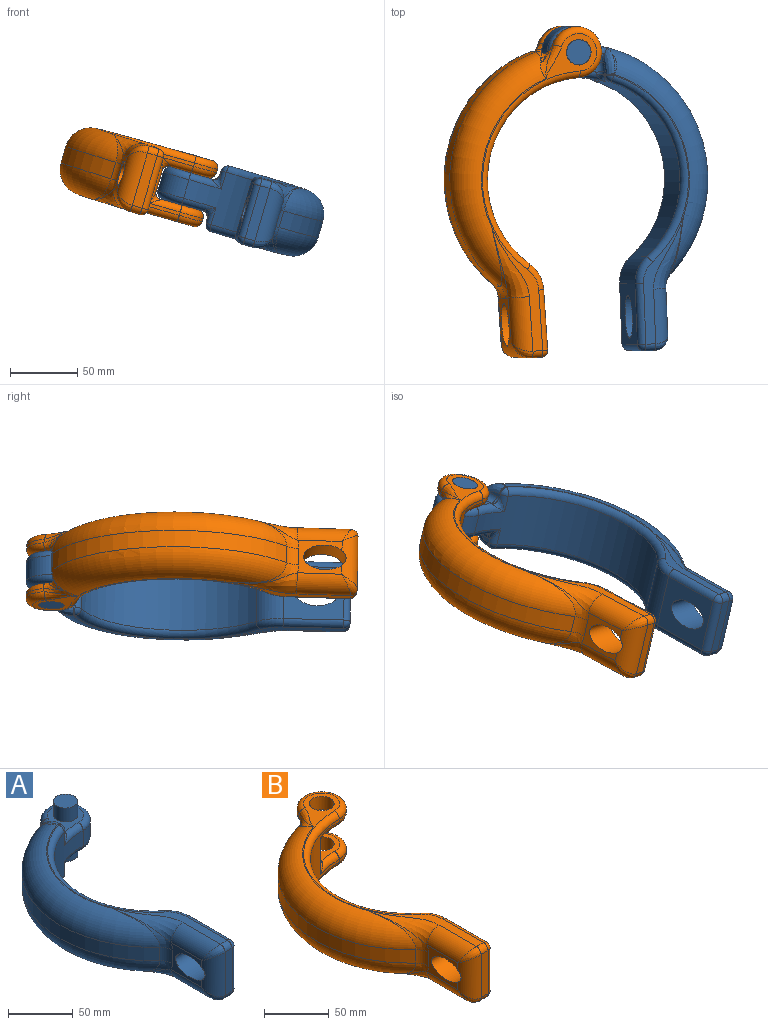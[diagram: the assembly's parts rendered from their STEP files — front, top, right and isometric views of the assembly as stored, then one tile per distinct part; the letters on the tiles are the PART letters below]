
ASSEMBLY  parts=2 mates=1
PART A: 72 faces, bbox 130.1x245.4x76.2 mm
  f0: bspline ~8.17x6.54mm, area 11.9mm2, adj f5,f15,f17,f42
  f1: bspline ~24.13x21.85mm, area 0mm2, adj f16,f52
  f2: plane 202.03x55.42mm, normal (0,0,1), area 673.6mm2, adj f8,f16,f21,f23,f26,f33,f35,f50
  f3: plane 202.03x55.42mm, normal (0,0,-1), area 673.6mm2, adj f9,f15,f18,f20,f28,f30,f37,f57
  f4: cylinder r=76.2mm len=135.68mm, axis (0,0,-1), area 6970.8mm2, adj f5,f8,f9,f36,f44,f47,f48,f53
  f5: cylinder r=19.05mm len=38.1mm, axis (0,0,-1), area 1159.1mm2, adj f0,f4,f7,f17,f43,f46
  f6: bspline ~24.13x21.85mm, area 0mm2, adj f15,f54
  f7: bspline ~8.17x6.54mm, area 10.7mm2, adj f5,f16,f17,f45
  f8: torus R=81.28mm, axis (0,0,1), area 1328mm2, adj f2,f4,f35,f49
  f9: torus R=81.28mm, axis (0,0,1), area 1328mm2, adj f3,f4,f37,f55
  f10: plane 45.1x40.64mm, normal (1,0,0), area 1347.7mm2, adj f14,f26,f27,f28,f36
  f11: cylinder r=101.12mm len=173.13mm, axis (0,0,-1), area 2773.9mm2, adj f15,f16,f17,f24
  f12: plane 33.12x25.41mm, normal (-1,0,0), area 362.8mm2, adj f14,f18,f19,f21,f22,f24,f25
  f13: plane 40.64x7.62mm, normal (0,-1,0), area 309.7mm2, adj f19,f27,f30,f33
  f14: extruded ~31.75x25.4mm, area 2069.9mm2, adj f10,f12,f19
  f15: torus R=82.07mm, axis (0,0,1), area 5601.8mm2, adj f0,f3,f6,f11,f22,f42,f54,f56
  f16: torus R=82.07mm, axis (0,0,1), area 5601.6mm2, adj f1,f2,f7,f11,f25,f45,f51,f52
  f17: cylinder r=12.7mm len=12.7mm, axis (0,0,1), area 133.5mm2, adj f0,f5,f7,f11
  f18: cylinder r=12.7mm len=40.73mm, axis (0,-1,0), area 736.6mm2, adj f3,f12,f20,f29
  f19: cylinder r=12.7mm len=40.64mm, axis (0,0,-1), area 640mm2, adj f12,f13,f14,f29,f32
  f20: bspline ~56.17x25.4mm, area 0mm2, adj f3,f18,f22
  f21: cylinder r=12.7mm len=40.73mm, axis (0,1,0), area 736.6mm2, adj f2,f12,f23,f32
  f22: bspline ~56.94x34.14mm, area 144.1mm2, adj f12,f15,f20,f24
  f23: bspline ~56.17x25.4mm, area 342.2mm2, adj f2,f21,f25
  f24: cylinder r=12.7mm len=12.7mm, axis (0,0,-1), area 135mm2, adj f11,f12,f22,f25
  f25: bspline ~56.94x34.14mm, area 144.1mm2, adj f12,f16,f23,f24
  f26: cylinder r=5.08mm len=45.1mm, axis (0,-1,0), area 359.9mm2, adj f2,f10,f34,f35
  f27: cylinder r=5.08mm len=40.64mm, axis (0,0,-1), area 324.3mm2, adj f10,f13,f31,f34
  f28: cylinder r=5.08mm len=45.1mm, axis (0,1,0), area 359.9mm2, adj f3,f10,f31,f37
  f29: bspline ~13.28x12.7mm, area 69.9mm2, adj f18,f19,f30
  f30: cylinder r=5.08mm len=7.62mm, axis (1,0,0), area 60.8mm2, adj f3,f13,f29,f31
  f31: sphere r=5.08mm, area 40.5mm2, adj f27,f28,f30
  f32: bspline ~13.28x12.7mm, area 69.9mm2, adj f19,f21,f33
  f33: cylinder r=5.08mm len=7.62mm, axis (-1,0,0), area 60.8mm2, adj f2,f13,f32,f34
  f34: sphere r=5.08mm, area 40.5mm2, adj f26,f27,f33
  f35: torus R=20.32mm, axis (0,0,1), area 168.3mm2, adj f2,f8,f26,f36
  f36: cylinder r=25.4mm len=40.64mm, axis (0,0,-1), area 924.6mm2, adj f4,f10,f35,f37
  f37: torus R=20.32mm, axis (0,0,1), area 168.3mm2, adj f3,f9,f28,f36
  f38: plane 32.63x29.63mm, normal (0,0,-1), area 441.6mm2, adj f42,f43,f44,f60,f61,f70
  f39: plane 9.95x3.29mm, normal (1,0,0), area 21.5mm2, adj f53,f54,f56,f57,f59,f60
  f40: plane 32.61x29.63mm, normal (0,0,1), area 441.5mm2, adj f45,f46,f47,f65,f66,f69
  f41: plane 10.06x3.38mm, normal (1,0,0), area 22.4mm2, adj f48,f50,f51,f52,f64,f65
  f42: bspline ~15.02x12.96mm, area 76.6mm2, adj f0,f15,f38,f43,f62
  f43: torus R=13.97mm, axis (0,0,1), area 579mm2, adj f5,f38,f42,f44
  f44: torus R=81.28mm, axis (0,0,1), area 156.2mm2, adj f4,f38,f43,f58,f59
  f45: bspline ~15.01x12.95mm, area 76.4mm2, adj f7,f16,f40,f46,f67
  f46: torus R=13.97mm, axis (0,0,1), area 579mm2, adj f5,f40,f45,f47
  f47: torus R=81.28mm, axis (0,0,1), area 156.2mm2, adj f4,f40,f46,f63,f64
  f48: cylinder r=5.08mm len=13.15mm, axis (0,0,-1), area 51.9mm2, adj f4,f41,f49,f63
  f49: sphere r=5.08mm, area 33.8mm2, adj f8,f48,f50
  f50: cylinder r=5.08mm len=5.08mm, axis (0,1,0), area 6.6mm2, adj f2,f41,f49,f51
  f51: bspline ~5.16x5.15mm, area 2.4mm2, adj f16,f41,f50,f52
  f52: bspline ~21.69x18.52mm, area 173.6mm2, adj f1,f16,f41,f51,f66,f67
  f53: cylinder r=5.08mm len=13.06mm, axis (0,0,-1), area 51.3mm2, adj f4,f39,f55,f58
  f54: bspline ~21.69x18.52mm, area 172.7mm2, adj f6,f15,f39,f56,f61,f62
  f55: sphere r=5.08mm, area 31.9mm2, adj f9,f53,f57
  f56: bspline ~5.16x5.15mm, area 2.4mm2, adj f15,f39,f54,f57
  f57: cylinder r=5.08mm len=5.08mm, axis (0,-1,0), area 6.6mm2, adj f3,f39,f55,f56
  f58: bspline ~10.11x8.27mm, area 24.8mm2, adj f44,f53,f59
  f59: bspline ~5.31x5.2mm, area 15.5mm2, adj f39,f44,f58,f60
  f60: cylinder r=5.08mm len=7.13mm, axis (0,-1,0), area 56.9mm2, adj f38,f39,f59,f61
  f61: bspline ~10.65x6.87mm, area 50.2mm2, adj f38,f54,f60,f62
  f62: bspline ~8.65x7.7mm, area 31.8mm2, adj f15,f42,f54,f61
  f63: bspline ~10.11x8.27mm, area 24.7mm2, adj f47,f48,f64
  f64: bspline ~5.45x5.2mm, area 15.5mm2, adj f41,f47,f63,f65
  f65: cylinder r=5.08mm len=7.24mm, axis (0,1,0), area 57.8mm2, adj f40,f41,f64,f66
  f66: bspline ~11.83x6.86mm, area 49.6mm2, adj f40,f52,f65,f67
  f67: bspline ~8.66x7.75mm, area 32.1mm2, adj f16,f45,f52,f66
  f68: plane 18.64x18.64mm, normal (0,0,1), area 273mm2, adj f69
  f69: cylinder r=9.32mm len=18.64mm, axis (0,0,-1), area 770.3mm2, adj f40,f68
  f70: cylinder r=9.32mm len=18.64mm, axis (0,0,-1), area 765mm2, adj f38,f71
  f71: plane 18.64x18.64mm, normal (0,0,-1), area 273mm2, adj f70
PART B: 69 faces, bbox 135.1x250.4x81.2 mm
  f0: cylinder r=76.2mm len=135.68mm, axis (0,0,-1), area 6732.8mm2, adj f1,f7,f25,f29,f39,f45,f48,f56
  f1: cylinder r=19.05mm len=38.1mm, axis (0,0,-1), area 213.1mm2, adj f0,f2,f24,f46
  f2: bspline ~26.1x25.43mm, area 86.5mm2, adj f1,f13,f23,f47,f55
  f3: cylinder r=9.53mm len=19.05mm, axis (0,0,1), area 762.8mm2, adj f4,f43
  f4: plane 238.62x101.03mm, normal (0,0,1), area 1173.7mm2, adj f3,f13,f18,f20,f23,f24,f25,f26
  f5: plane 233.63x96.04mm, normal (0,0,-1), area 1173.7mm2, adj f12,f15,f17,f28,f29,f30,f31,f33
  f6: plane 45.1x40.64mm, normal (1,0,0), area 1357.8mm2, adj f11,f26,f27,f28,f39
  f7: cylinder r=19.05mm len=38.1mm, axis (0,0,-1), area 205.7mm2, adj f0,f14,f30,f49
  f8: cylinder r=101.12mm len=172.26mm, axis (0,0,-1), area 2731.3mm2, adj f12,f13,f21,f53
  f9: plane 33.12x25.41mm, normal (-1,0,0), area 372.4mm2, adj f11,f15,f16,f18,f19,f21,f22
  f10: plane 40.64x7.62mm, normal (0,-1,0), area 309.7mm2, adj f16,f27,f33,f36
  f11: extruded ~31.75x25.4mm, area 2056mm2, adj f6,f9,f16
  f12: torus R=82.07mm, axis (0,0,1), area 5583.1mm2, adj f5,f8,f14,f19,f52
  f13: torus R=82.07mm, axis (0,0,1), area 5583.1mm2, adj f2,f4,f8,f22,f54
  f14: bspline ~26.1x25.43mm, area 84.6mm2, adj f7,f12,f31,f50,f51
  f15: cylinder r=12.7mm len=40.73mm, axis (0,-1,0), area 736.6mm2, adj f5,f9,f17,f32
  f16: cylinder r=12.7mm len=40.64mm, axis (0,0,-1), area 640.4mm2, adj f9,f10,f11,f32,f35
  f17: bspline ~56.17x25.4mm, area 0mm2, adj f5,f15,f19
  f18: cylinder r=12.7mm len=40.73mm, axis (0,1,0), area 736.6mm2, adj f4,f9,f20,f35
  f19: bspline ~56.94x34.14mm, area 144.1mm2, adj f9,f12,f17,f21
  f20: bspline ~56.17x25.4mm, area 342.2mm2, adj f4,f18,f22
  f21: cylinder r=12.7mm len=12.7mm, axis (0,0,-1), area 135mm2, adj f8,f9,f19,f22
  f22: bspline ~56.94x34.14mm, area 144.1mm2, adj f9,f13,f20,f21
  f23: bspline ~26.65x14.35mm, area 73.4mm2, adj f2,f4,f24
  f24: torus R=13.97mm, axis (0,0,1), area 597.1mm2, adj f1,f4,f23,f25
  f25: torus R=81.28mm, axis (0,0,1), area 1536.1mm2, adj f0,f4,f24,f38
  f26: cylinder r=5.08mm len=45.1mm, axis (0,-1,0), area 359.9mm2, adj f4,f6,f37,f38
  f27: cylinder r=5.08mm len=40.64mm, axis (0,0,-1), area 324.3mm2, adj f6,f10,f34,f37
  f28: cylinder r=5.08mm len=45.1mm, axis (0,1,0), area 359.9mm2, adj f5,f6,f34,f40
  f29: torus R=81.28mm, axis (0,0,1), area 1536.1mm2, adj f0,f5,f30,f40
  f30: torus R=13.97mm, axis (0,0,1), area 597.1mm2, adj f5,f7,f29,f31
  f31: bspline ~26.65x14.35mm, area 115.4mm2, adj f5,f14,f30
  f32: bspline ~13.28x12.7mm, area 69.9mm2, adj f15,f16,f33
  f33: cylinder r=5.08mm len=7.62mm, axis (1,0,0), area 60.8mm2, adj f5,f10,f32,f34
  f34: sphere r=5.08mm, area 40.5mm2, adj f27,f28,f33
  f35: bspline ~13.28x12.7mm, area 69.9mm2, adj f16,f18,f36
  f36: cylinder r=5.08mm len=7.62mm, axis (-1,0,0), area 60.8mm2, adj f4,f10,f35,f37
  f37: sphere r=5.08mm, area 40.5mm2, adj f26,f27,f36
  f38: torus R=20.32mm, axis (0,0,1), area 168.3mm2, adj f4,f25,f26,f39
  f39: cylinder r=25.4mm len=40.64mm, axis (0,0,-1), area 924.6mm2, adj f0,f6,f38,f40
  f40: torus R=20.32mm, axis (0,0,1), area 168.3mm2, adj f5,f28,f29,f39
  f41: cylinder r=9.53mm len=19.05mm, axis (0,0,1), area 757.3mm2, adj f5,f44
  f42: plane 16x15.48mm, normal (1,0,0), area 236.5mm2, adj f52,f53,f54,f56,f58,f59,f64,f65
  f43: plane 30.72x29.63mm, normal (0,0,-1), area 418.7mm2, adj f3,f45,f46,f47,f65,f66
  f44: plane 30.72x29.63mm, normal (0,0,1), area 418.6mm2, adj f41,f48,f49,f50,f59,f60
  f45: torus R=81.28mm, axis (0,0,-1), area 156.2mm2, adj f0,f43,f46,f63,f64
  f46: torus R=13.97mm, axis (0,0,-1), area 591mm2, adj f1,f43,f45,f47
  f47: bspline ~21.15x18.45mm, area 59.5mm2, adj f2,f43,f46,f67,f68
  f48: torus R=81.28mm, axis (0,0,-1), area 156.2mm2, adj f0,f44,f49,f57,f58
  f49: torus R=13.97mm, axis (0,0,-1), area 591.2mm2, adj f7,f44,f48,f50
  f50: bspline ~20.84x17.43mm, area 59.5mm2, adj f14,f44,f49,f61,f62
  f51: bspline ~9.5x9.08mm, area 2.5mm2, adj f14,f52,f62
  f52: bspline ~13.56x9.97mm, area 43.6mm2, adj f12,f42,f51,f53,f60,f61
  f53: cylinder r=5.08mm len=12.7mm, axis (0,0,-1), area 119.5mm2, adj f8,f42,f52,f54
  f54: bspline ~15.61x9.97mm, area 42.9mm2, adj f13,f42,f53,f55,f66,f67
  f55: bspline ~10.45x9.83mm, area 2.3mm2, adj f2,f54,f68
  f56: cylinder r=5.08mm len=35.56mm, axis (0,0,-1), area 161.9mm2, adj f0,f42,f57,f63
  f57: bspline ~10.11x8.27mm, area 24.7mm2, adj f48,f56,f58
  f58: bspline ~5.45x5.2mm, area 15.5mm2, adj f42,f48,f57,f59
  f59: cylinder r=5.08mm len=12.61mm, axis (0,1,0), area 100.6mm2, adj f42,f44,f58,f60
  f60: bspline ~6.73x5.73mm, area 12.5mm2, adj f44,f52,f59,f61
  f61: bspline ~12.35x10.61mm, area 76mm2, adj f50,f52,f60,f62
  f62: bspline ~4.76x4.06mm, area 6.7mm2, adj f50,f51,f61
  f63: bspline ~10.11x8.27mm, area 24.8mm2, adj f45,f56,f64
  f64: bspline ~5.45x5.2mm, area 15.5mm2, adj f42,f45,f63,f65
  f65: cylinder r=5.08mm len=12.62mm, axis (0,-1,0), area 100.7mm2, adj f42,f43,f64,f66
  f66: bspline ~6.75x5.72mm, area 12.6mm2, adj f43,f54,f65,f67
  f67: bspline ~12.39x10.62mm, area 76mm2, adj f47,f54,f66,f68
  f68: bspline ~5.1x4.5mm, area 6.3mm2, adj f47,f55,f67
PLACE A rot(axis=(0.02,-1,-0.01),163.8deg) t=(-40.01,-6.86,66.57)mm
PLACE B rot(axis=(0.08,0.97,0.24),16.7deg) t=(-51.66,-6.07,17.06)mm
MATE revolute A.f69 <-> B.f3  axis (0.28,-0.01,0.96) through (-43.76,88.29,68.89)mm
